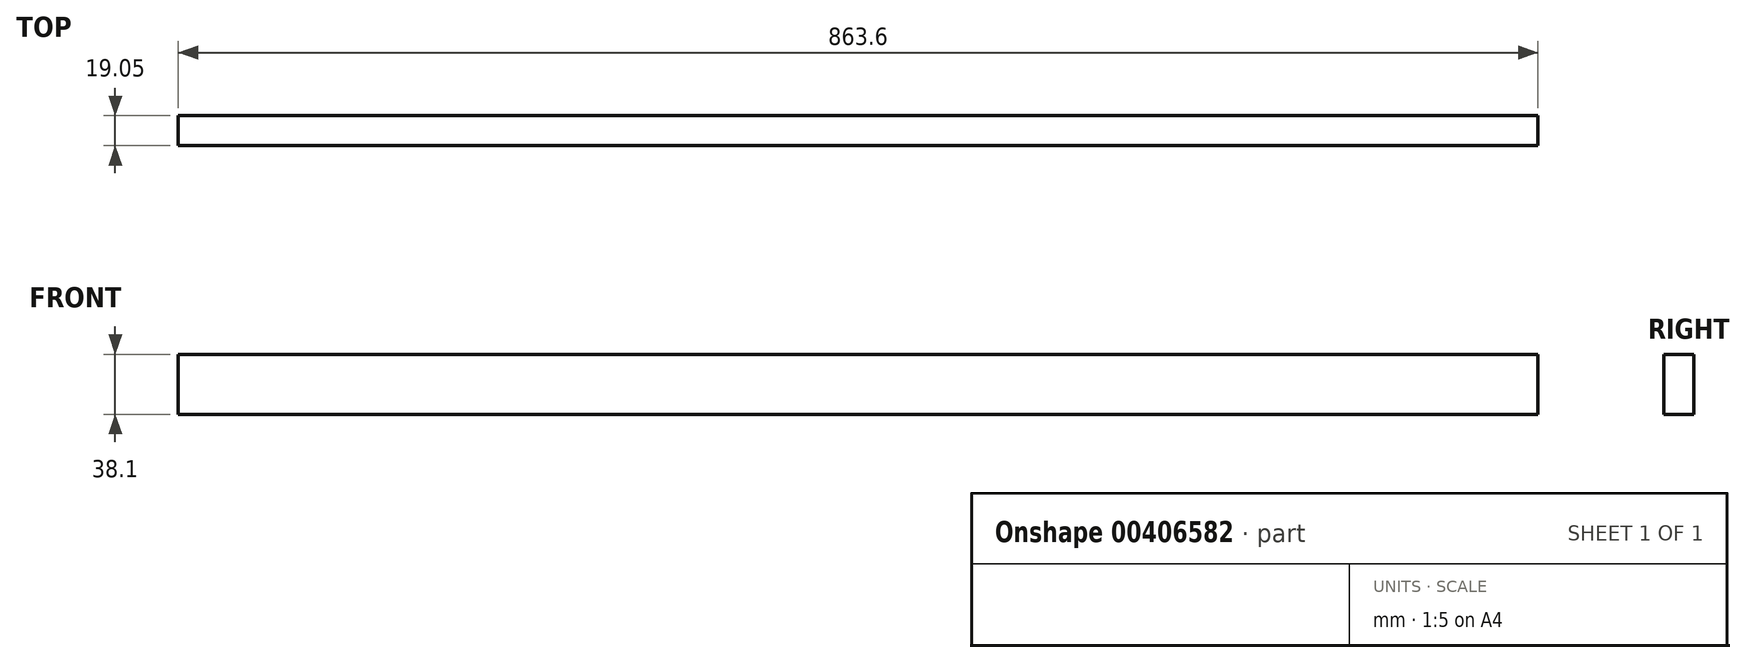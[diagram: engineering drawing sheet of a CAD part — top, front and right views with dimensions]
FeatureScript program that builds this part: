
annotation { "Feature Type Name" : "Feature", "Feature Type Description" : "" }
export const myFeature = defineFeature(function(context is Context, id is Id, definition is map)
    precondition{}
    {
        {
            var Q0;
            Q0=qCreatedBy(makeId("Front.planeOp"),FACE);
            var sketch = newSketch(context, id + "F0", { "sketchPlane" : qUnion([Q0])});
            skLineSegment(sketch, "E0", {"start": v(0, 0) * mm, "end": v(863.6, 0) * mm});
            skLineSegment(sketch, "E1", {"start": v(863.6, 0) * mm, "end": v(863.6, -19.05) * mm});
            skLineSegment(sketch, "E2", {"start": v(863.6, -19.05) * mm, "end": v(863.6, -19.05) * mm});
            skLineSegment(sketch, "E3", {"start": v(863.6, -19.05) * mm, "end": v(863.6, -38.1) * mm});
            skLineSegment(sketch, "E4", {"start": v(863.6, -38.1) * mm, "end": v(0, -38.1) * mm});
            skLineSegment(sketch, "E5", {"start": v(0, -19.05) * mm, "end": v(0, -19.05) * mm});
            skLineSegment(sketch, "E6", {"start": v(0, -38.1) * mm, "end": v(0, 0) * mm});
            skSolve(sketch);
        }
        {
            var Q0;
            Q0=makeQuery(id+"F0.imprint","IMPRINT",FACE,{"disambiguationData":[TD([[makeQuery(id+"F0.imprint","IMPRINT",EDGE,{"derivedFrom":sQuery(id+"F0.wireOp",EDGE,"E0")}),-1.0]])]});
            extrude(context, id + "F1", {"entities" : qUnion([Q0]), "depth" : 19.05 * mm});
        }
    });
